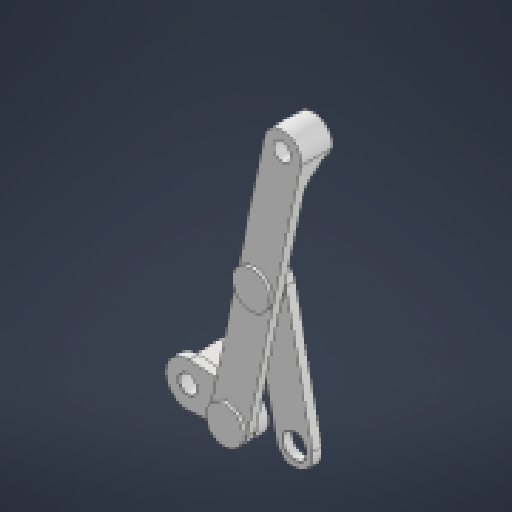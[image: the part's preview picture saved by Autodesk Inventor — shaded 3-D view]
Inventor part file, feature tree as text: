
AUTODESK INVENTOR PART (.ipt)
format: ipt  version: 2024.1 (Build 281209000, 209)  size: 268,800 bytes
history: native  units: in
note: dims shown in document units (in); Inventor stores cm internally (conversion verified against a paired STEP export)
features: extrude x9, sketch x6, projected_geometry x6, other x5, reference x4, chamfer x2, fillet x1
ambient origin geometry x8: Origin, YZ Plane, XZ Plane, XY Plane, X Axis, Y Axis, Z Axis, Center Point
bodies: Solid1 (feature_tree)
feature tree (33):
  sketch  "Sketch1"  dims[d0=0.25in d1=0.25in]
  extrude  "Extrusion1"  Depth=0.25in
  extrude  "Extrusion2"  Depth=0.0625in
  chamfer  "Chamfer1"  Distance=0.0625in
  extrude  "Extrusion3"  Depth=0.277in TaperAngle=0.0deg
  sketch  "Sketch3"  dims[d6=0.002in d7=0.277in d8=0.0in]
  extrude  "Extrusion4"  Depth=0.125in TaperAngle=0.0deg
  extrude  "Extrusion5"  Depth=0.15in
  extrude  "Extrusion6"  Depth=0.15in
  extrude  "Extrusion7"  Depth=0.15in
  extrude  "Extrusion8"  Depth=0.15in
  chamfer  "Chamfer2"  Distance=0.0625in
  extrude  "Extrusion9"  Depth=0.15in TaperAngle=0.0deg
  fillet  "Fillet1"  Radius=0.0938in
  reference  "Reference1"
  reference  "Reference2"
  reference  "Reference3"
  sketch  "Sketch2"  dims[d2=0.25in d3=0.16in d4=0.0625in d5=0.0in]
  projected_geometry  "Projected Loop1"
  projected_geometry  "Projected Loop2"
  projected_geometry  "Projected Loop3"
  projected_geometry  "Projected Loop4"
  sketch  "Sketch4"  dims[d9=0.005in d10=0.125in d11=45.0deg d12=0.02in d13=0.0in]
  projected_geometry  "Projected Loop5"
  sketch  "Sketch5"  dims[d14=0.15in d15=0.15in]
  sketch  "Sketch6"  dims[d16=0.005in d17=0.005in d18=0.25in d20=0.12in d21=0.0625in d22=0.0in d23=0.008in d24=0.0in d25=0.0938in d26=0.0in d27=0.25in d28=0.25in d29=0.0233in d30=0.0in d31=0.12in d32=0.0in d33=0.0in d34=0.005in d35=0.125in d36=45.0deg d37=0.15in d38=0.0in d39=0.15in]
  reference  "Reference4"
  projected_geometry  "Projected Loop6"
  other  "<userpath>\Documents\School\FallCAD\Bio\Bio.iam"
  other  "Bio.iam"
  other  "Bio12tNew:1"
  other  "Alignment:1"
  other  "FrontLinkage_MIR:1"
